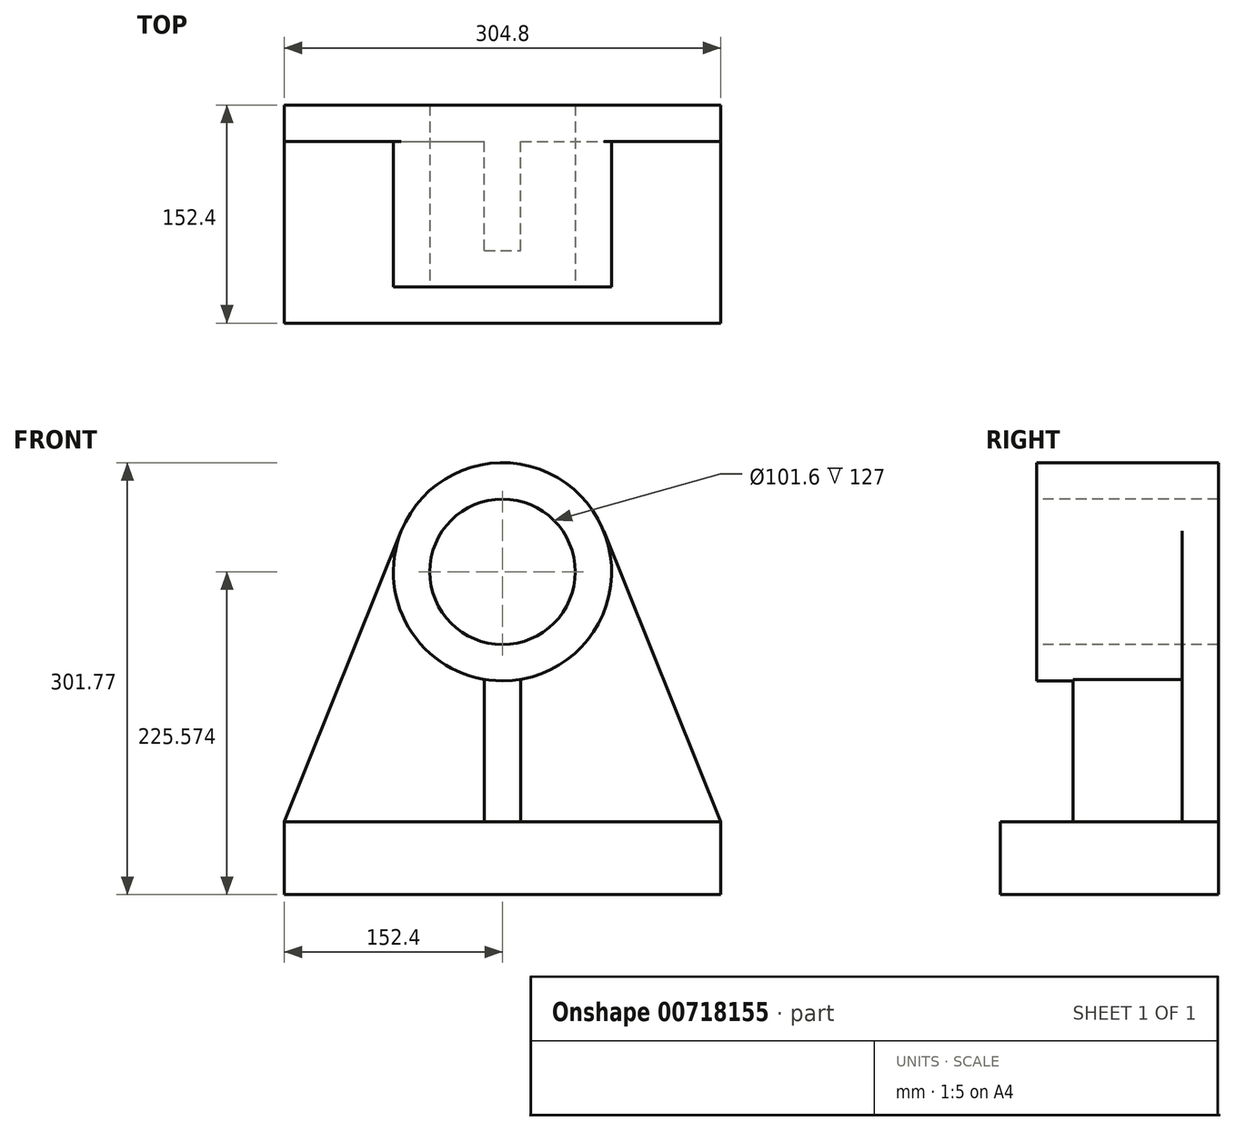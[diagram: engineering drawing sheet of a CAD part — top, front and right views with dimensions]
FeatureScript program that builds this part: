
annotation { "Feature Type Name" : "Feature", "Feature Type Description" : "" }
export const myFeature = defineFeature(function(context is Context, id is Id, definition is map)
    precondition{}
    {
        {
            var Q0;
            Q0=qCreatedBy(makeId("Front.planeOp"),FACE);
            var sketch = newSketch(context, id + "F0", { "sketchPlane" : qUnion([Q0])});
            skLineSegment(sketch, "E0.bottom", {"start": v(0, 0) * mm, "end": v(304.8, 0) * mm});
            skLineSegment(sketch, "E0.left", {"start": v(0, 0) * mm, "end": v(0, 50.8) * mm});
            skLineSegment(sketch, "E0.right", {"start": v(304.8, 0) * mm, "end": v(304.8, 50.8) * mm});
            skLineSegment(sketch, "E1", {"start": v(0, 50.8) * mm, "end": v(81.7, 254) * mm});
            skLineSegment(sketch, "E2", {"start": v(304.8, 50.8) * mm, "end": v(223.1, 254) * mm});
            skArc(sketch, "E3", {"start": v(223.1, 254) * mm, "mid": v(152.4, 301.77) * mm, "end": v(81.7, 254) * mm});
            skSolve(sketch);
        }
        {
            var Q0;
            Q0=makeQuery(id+"F0.imprint","IMPRINT",FACE,{"disambiguationData":[TD([[makeQuery(id+"F0.imprint","IMPRINT",EDGE,{"derivedFrom":sQuery(id+"F0.wireOp",EDGE,"E0.bottom")}),1.0]])]});
            extrude(context, id + "F1", {"entities" : qUnion([Q0]), "depth" : 25.4 * mm, "offsetDistance" : 25.4 * mm});
        }
        {
            var Q0;
            Q0=makeQuery(id+"F1.opExtrude","CAP_FACE",FACE,{"disambiguationData":[OSD([sQuery(id+"F0.wireOp",EDGE,"E0.bottom"),sQuery(id+"F0.wireOp",EDGE,"E0.left"),sQuery(id+"F0.wireOp",EDGE,"E0.right"),sQuery(id+"F0.wireOp",EDGE,"E1"),sQuery(id+"F0.wireOp",EDGE,"E2"),sQuery(id+"F0.wireOp",EDGE,"E3")])],"isStart":false});
            var sketch = newSketch(context, id + "F2", { "sketchPlane" : qUnion([Q0])});
            skLineSegment(sketch, "E4.bottom", {"start": v(0, 0) * mm, "end": v(304.8, 0) * mm});
            skLineSegment(sketch, "E4.top", {"start": v(0, 50.8) * mm, "end": v(304.8, 50.8) * mm});
            skLineSegment(sketch, "E4.left", {"start": v(0, 0) * mm, "end": v(0, 50.8) * mm});
            skLineSegment(sketch, "E4.right", {"start": v(304.8, 0) * mm, "end": v(304.8, 50.8) * mm});
            skSolve(sketch);
        }
        {
            var Q0;
            Q0=makeQuery(id+"F2.imprint","IMPRINT",FACE,{"disambiguationData":[TD([[makeQuery(id+"F2.imprint","IMPRINT",EDGE,{"derivedFrom":sQuery(id+"F2.wireOp",EDGE,"E4.bottom")}),1.0]])]});
            extrude(context, id + "F3", {"entities" : qUnion([Q0]), "operationType" : NewBodyOperationType.ADD, "depth" : 127 * mm, "offsetDistance" : 25.4 * mm});
        }
        {
            var Q0;
            Q0=makeQuery(id+"F1.opExtrude","CAP_FACE",FACE,{"disambiguationData":[OSD([sQuery(id+"F0.wireOp",EDGE,"E0.bottom"),sQuery(id+"F0.wireOp",EDGE,"E0.left"),sQuery(id+"F0.wireOp",EDGE,"E0.right"),sQuery(id+"F0.wireOp",EDGE,"E1"),sQuery(id+"F0.wireOp",EDGE,"E2"),sQuery(id+"F0.wireOp",EDGE,"E3")])],"isStart":false});
            var sketch = newSketch(context, id + "F4", { "sketchPlane" : qUnion([Q0])});
            skCircle(sketch, "E5", {"center": v(152.4, 225.57) * mm, "radius": 76.2 * mm});
            skSolve(sketch);
        }
        {
            var Q0;
            Q0=makeQuery(id+"F1.opExtrude","CAP_FACE",FACE,{"disambiguationData":[OSD([sQuery(id+"F0.wireOp",EDGE,"E0.bottom"),sQuery(id+"F0.wireOp",EDGE,"E0.left"),sQuery(id+"F0.wireOp",EDGE,"E0.right"),sQuery(id+"F0.wireOp",EDGE,"E1"),sQuery(id+"F0.wireOp",EDGE,"E2"),sQuery(id+"F0.wireOp",EDGE,"E3")])],"isStart":false});
            var sketch = newSketch(context, id + "F5", { "sketchPlane" : qUnion([Q0])});
            skCircle(sketch, "E6", {"center": v(152.4, 225.57) * mm, "radius": 50.8 * mm});
            skSolve(sketch);
        }
        {
            var Q0;
            Q0 = qSketchRegion(id + "F5", true);
            extrude(context, id + "F6", {"entities" : qUnion([Q0]), "operationType" : NewBodyOperationType.REMOVE, "endBound" : BoundingType.THROUGH_ALL, "oppositeDirection" : true, "depth" : 25.4 * mm, "offsetDistance" : 25.4 * mm});
        }
        {
            var Q0;
            {var subQ0=sQuery(id+"F4.wireOp",EDGE,"E5");var subQ1=makeQuery(id+"F4.imprint","INTERSECT",VERTEX,{"derivedFrom":[makeQuery(id+"F1.opExtrude","CAP_EDGE",EDGE,{"disambiguationData":[OSD([sQuery(id+"F0.wireOp",EDGE,"E1")])],"isStart":false}),subQ0]});Q0=makeQuery(id+"F4.imprint","IMPRINT",FACE,{"disambiguationData":[TD([[makeQuery(id+"F4.imprint","IMPRINT",EDGE,{"disambiguationData":[TD([[subQ1,1.0]])],"derivedFrom":subQ0}),1.0]])]});}
            extrude(context, id + "F7", {"entities" : qUnion([Q0]), "operationType" : NewBodyOperationType.ADD, "depth" : 101.6 * mm, "offsetDistance" : 25.4 * mm});
        }
        {
            var Q0;
            Q0 = qSketchRegion(id + "F5", true);
            extrude(context, id + "F8", {"entities" : qUnion([Q0]), "operationType" : NewBodyOperationType.REMOVE, "endBound" : BoundingType.THROUGH_ALL, "depth" : 25.4 * mm, "offsetDistance" : 25.4 * mm, "hasSecondDirection" : true, "secondDirectionBound" : SecondDirectionBoundingType.THROUGH_ALL, "secondDirectionOppositeDirection" : true, "secondDirectionDepth" : 25.4 * mm});
        }
        {
            var Q0;
            Q0=makeQuery(id+"F1.opExtrude","CAP_FACE",FACE,{"disambiguationData":[OSD([sQuery(id+"F0.wireOp",EDGE,"E0.bottom"),sQuery(id+"F0.wireOp",EDGE,"E0.left"),sQuery(id+"F0.wireOp",EDGE,"E0.right"),sQuery(id+"F0.wireOp",EDGE,"E1"),sQuery(id+"F0.wireOp",EDGE,"E2"),sQuery(id+"F0.wireOp",EDGE,"E3")])],"isStart":false});
            var sketch = newSketch(context, id + "F9", { "sketchPlane" : qUnion([Q0])});
            skLineSegment(sketch, "E7.bottom", {"start": v(139.7, 50.8) * mm, "end": v(165.1, 50.8) * mm});
            skLineSegment(sketch, "E7.left", {"start": v(139.7, 50.8) * mm, "end": v(139.7, 150.44) * mm});
            skLineSegment(sketch, "E7.right", {"start": v(165.1, 50.8) * mm, "end": v(165.1, 150.44) * mm});
            skArc(sketch, "E8", {"start": v(139.7, 150.44) * mm, "mid": v(152.4, 149.37) * mm, "end": v(165.1, 150.44) * mm});
            skLineSegment(sketch, "E9", {"start": v(152.4, 149.37) * mm, "end": v(152.4, 50.8) * mm, "construction": true});
            skPoint(sketch, "E9.startSnap0", {"position": v(152.4, 149.37) * mm});
            skSolve(sketch);
        }
        {
            var Q0;
            Q0 = qSketchRegion(id + "F9", true);
            extrude(context, id + "F10", {"entities" : qUnion([Q0]), "operationType" : NewBodyOperationType.ADD, "depth" : 76.2 * mm, "offsetDistance" : 25.4 * mm});
        }
    });
